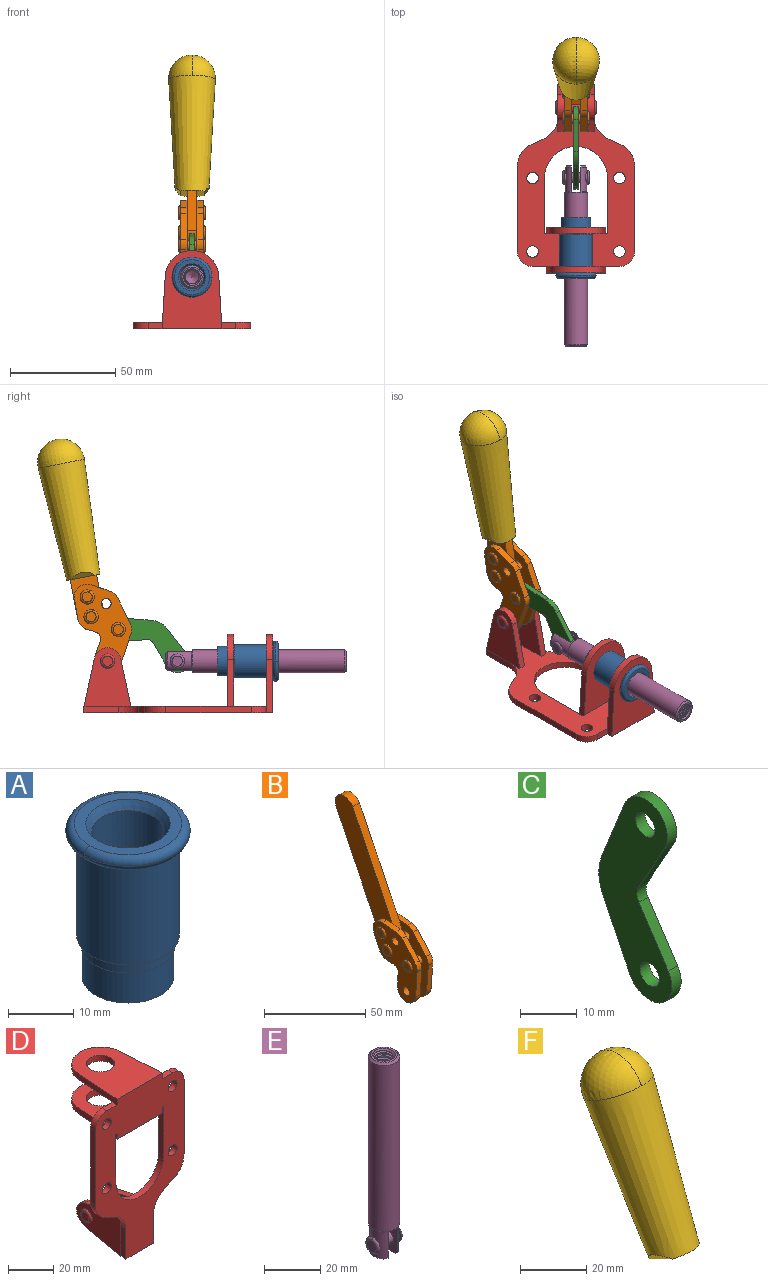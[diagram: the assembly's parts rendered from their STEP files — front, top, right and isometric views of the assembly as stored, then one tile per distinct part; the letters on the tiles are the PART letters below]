
ASSEMBLY  parts=6 mates=6
PART A: 15 faces, bbox 20.6x20.6x28.7 mm
  f0: torus R=8.26mm, axis (0,0,1), area 56.8mm2, adj f1,f10,f12
  f1: torus R=8.26mm, axis (0,0,1), area 56.8mm2, adj f0,f6,f13
  f2: cylinder r=5.59mm len=25.91mm, axis (0,0,1), area 909.6mm2, adj f3,f4
  f3: cone r=6.86mm half-angle=45deg, axis (0,0,-1), area 70.2mm2, adj f2,f14
  f4: cone r=6.47mm half-angle=30deg, axis (0,0,1), area 66.7mm2, adj f2,f13
  f5: cylinder r=7.04mm len=14.07mm, axis (0,0,1), area 252.6mm2, adj f11,f14
  f6: torus R=8.26mm, axis (0,0,1), area 56.8mm2, adj f1,f12,f13
  f7: cylinder r=7.16mm len=14.33mm, axis (0,0,1), area 91.5mm2, adj f9,f11
  f8: cylinder r=7.86mm len=18.42mm, axis (0,0,1), area 909.6mm2, adj f9,f10
  f9: plane 15.72x15.72mm, normal (0,0,-1), area 33mm2, adj f7,f8
  f10: plane 16.51x16.51mm, normal (0,0,-1), area 19.9mm2, adj f0,f8,f12
  f11: plane 14.33x14.33mm, normal (0,0,-1), area 5.7mm2, adj f5,f7
  f12: torus R=8.26mm, axis (0,0,1), area 56.8mm2, adj f0,f6,f10
  f13: plane 16.51x16.51mm, normal (0,0,1), area 82.7mm2, adj f1,f4,f6
  f14: plane 14.07x14.07mm, normal (0,0,-1), area 7.8mm2, adj f3,f5
PART B: 59 faces, bbox 12.9x60.2x99.6 mm
  f0: torus R=2.39mm, axis (-1,0,0), area 14.9mm2, adj f20,f43,f51
  f1: torus R=2.39mm, axis (-1,0,0), area 14.9mm2, adj f19,f42,f51
  f2: torus R=2.39mm, axis (-1,0,0), area 14.9mm2, adj f18,f35,f51
  f3: torus R=2.39mm, axis (-1,0,0), area 14.9mm2, adj f14,f17,f23
  f4: torus R=2.39mm, axis (-1,0,0), area 14.9mm2, adj f13,f16,f23
  f5: torus R=2.39mm, axis (-1,0,0), area 14.9mm2, adj f12,f15,f23
  f6: cylinder r=2.39mm len=4.78mm, axis (1,0,0), area 46.5mm2, adj f48,f50,f51
  f7: cylinder r=2.39mm len=4.78mm, axis (1,0,0), area 46.5mm2, adj f50,f51
  f8: cylinder r=6.35mm len=12.68mm, axis (1,0,0), area 61.8mm2, adj f38,f39,f50,f51
  f9: cylinder r=2.39mm len=4.78mm, axis (-1,0,0), area 70.5mm2, adj f46,f50
  f10: cylinder r=2.39mm len=4.78mm, axis (-1,0,0), area 46.5mm2, adj f23,f45,f46
  f11: cylinder r=2.39mm len=4.78mm, axis (-1,0,0), area 46.5mm2, adj f23,f46
  f12: plane 4.78x4.78mm, normal (1,0,0), area 17.9mm2, adj f5,f15
  f13: plane 4.78x4.78mm, normal (1,0,0), area 17.9mm2, adj f4,f16
  f14: plane 4.78x4.78mm, normal (1,0,0), area 17.9mm2, adj f3,f17
  f15: torus R=2.39mm, axis (-1,0,0), area 14.9mm2, adj f5,f12,f23
  f16: torus R=2.39mm, axis (-1,0,0), area 14.9mm2, adj f4,f13,f23
  f17: torus R=2.39mm, axis (-1,0,0), area 14.9mm2, adj f3,f14,f23
  f18: plane 4.78x4.78mm, normal (-1,0,0), area 17.9mm2, adj f2,f35
  f19: plane 4.78x4.78mm, normal (-1,0,0), area 17.9mm2, adj f1,f42
  f20: plane 4.78x4.78mm, normal (-1,0,0), area 17.9mm2, adj f0,f43
  f21: plane 2.26x0.2mm, normal (1,0,0), area 0.2mm2, adj f31,f44
  f22: plane 2.26x0.2mm, normal (-1,0,0), area 0.2mm2, adj f41,f44
  f23: plane 39.37x30.77mm, normal (1,0,0), area 565.5mm2, adj f3,f4,f5,f10,f11,f15,f16,f17
  f24: cylinder r=6.1mm len=4.15mm, axis (-1,0,0), area 14.7mm2, adj f23,f25,f32,f46
  f25: plane 10.25x9.01mm, normal (0,-0.75,0.66), area 42.3mm2, adj f23,f24,f26,f46
  f26: cylinder r=6.35mm len=4.64mm, axis (-1,0,0), area 15.6mm2, adj f23,f25,f27,f46
  f27: plane 15.84x3.1mm, normal (0,-1,-0.07), area 49.2mm2, adj f23,f26,f28,f46
  f28: cylinder r=6.35mm len=12.68mm, axis (-1,0,0), area 61.8mm2, adj f23,f27,f29,f46
  f29: plane 8.11x3.1mm, normal (0,1,0.07), area 25.2mm2, adj f23,f28,f30,f46
  f30: cylinder r=3.05mm len=3.25mm, axis (-1,0,0), area 14.8mm2, adj f23,f29,f31,f46
  f31: plane 5.99x3.1mm, normal (0,0.07,-1), area 18.6mm2, adj f21,f23,f30,f44,f46
  f32: plane 9.5x3.1mm, normal (0,-0.07,1), area 29.5mm2, adj f23,f24,f33,f46,f47
  f33: cylinder r=6.1mm len=8.63mm, axis (-1,0,0), area 39.1mm2, adj f23,f32,f34,f47
  f34: plane 8.65x3.96mm, normal (0,0.91,-0.42), area 29.5mm2, adj f23,f33,f44,f47
  f35: torus R=2.39mm, axis (-1,0,0), area 14.9mm2, adj f2,f18,f51
  f36: plane 10.25x9.01mm, normal (0,-0.75,0.66), area 42.3mm2, adj f37,f49,f50,f51
  f37: cylinder r=6.35mm len=4.64mm, axis (1,0,0), area 15.6mm2, adj f36,f38,f50,f51
  f38: plane 15.84x3.1mm, normal (0,-1,-0.07), area 49.2mm2, adj f8,f37,f50,f51
  f39: plane 8.11x3.1mm, normal (0,1,0.07), area 25.2mm2, adj f8,f40,f50,f51
  f40: cylinder r=3.05mm len=3.25mm, axis (1,0,0), area 14.8mm2, adj f39,f41,f50,f51
  f41: plane 5.99x3.1mm, normal (0,0.07,-1), area 18.6mm2, adj f22,f40,f44,f50,f51
  f42: torus R=2.39mm, axis (-1,0,0), area 14.9mm2, adj f1,f19,f51
  f43: torus R=2.39mm, axis (-1,0,0), area 14.9mm2, adj f0,f20,f51
  f44: cylinder r=6.35mm len=12.12mm, axis (-1,0,0), area 128.9mm2, adj f21,f22,f23,f31,f34,f41,f46,f47
  f45: plane 2.65x1.35mm, normal (1,0,0), area 1mm2, adj f10,f55
  f46: plane 39.08x20.42mm, normal (-1,0,0), area 412.5mm2, adj f9,f10,f11,f24,f25,f26,f27,f28
  f47: plane 77.62x39.82mm, normal (1,0,0), area 850mm2, adj f32,f33,f34,f44,f53,f54,f55
  f48: plane 2.65x1.35mm, normal (-1,0,0), area 1mm2, adj f6,f55
  f49: cylinder r=6.1mm len=4.15mm, axis (1,0,0), area 14.7mm2, adj f36,f50,f51,f56
  f50: plane 39.08x20.42mm, normal (1,0,0), area 412.5mm2, adj f6,f7,f8,f9,f36,f37,f38,f39
  f51: plane 39.37x30.77mm, normal (-1,0,0), area 565.5mm2, adj f0,f1,f2,f6,f7,f8,f35,f36
  f52: plane 8.65x3.96mm, normal (0,0.91,-0.42), area 29.5mm2, adj f44,f51,f57,f58
  f53: plane 68.49x33.4mm, normal (0,0.9,-0.44), area 358.1mm2, adj f44,f47,f54,f58
  f54: cylinder r=6.35mm len=12.06mm, axis (1,0,0), area 93.7mm2, adj f47,f53,f55,f58
  f55: plane 68.49x33.4mm, normal (0,-0.9,0.44), area 358.1mm2, adj f44,f45,f46,f47,f48,f50,f54,f58
  f56: plane 9.5x3.1mm, normal (0,-0.07,1), area 29.5mm2, adj f49,f50,f51,f57,f58
  f57: cylinder r=6.1mm len=8.63mm, axis (1,0,0), area 39.1mm2, adj f51,f52,f56,f58
  f58: plane 77.62x39.82mm, normal (-1,0,0), area 850mm2, adj f44,f52,f53,f54,f55,f56,f57
PART C: 12 faces, bbox 2.3x18.2x42.8 mm
  f0: cylinder r=2.4mm len=4.8mm, axis (1,0,0), area 34.9mm2, adj f4,f11
  f1: cylinder r=10.41mm len=8.47mm, axis (1,0,0), area 20.2mm2, adj f4,f9,f10,f11
  f2: cylinder r=3.05mm len=3.16mm, axis (1,0,0), area 7.7mm2, adj f4,f6,f7,f11
  f3: cylinder r=2.4mm len=4.8mm, axis (1,0,0), area 34.9mm2, adj f4,f11
  f4: plane 42.81x18.23mm, normal (-1,0,0), area 414.1mm2, adj f0,f1,f2,f3,f5,f6,f7,f8
  f5: cylinder r=5.54mm len=10.67mm, axis (1,0,0), area 41.8mm2, adj f4,f6,f10,f11
  f6: plane 11.66x6.53mm, normal (0,-0.87,-0.49), area 30.9mm2, adj f2,f4,f5,f11
  f7: plane 11.17x7.33mm, normal (0,-0.84,0.55), area 30.9mm2, adj f2,f4,f8,f11
  f8: cylinder r=5.54mm len=10.51mm, axis (1,0,0), area 41.8mm2, adj f4,f7,f9,f11
  f9: plane 13.67x6.67mm, normal (0,0.9,-0.44), area 35.1mm2, adj f1,f4,f8,f11
  f10: plane 14.1x5.7mm, normal (0,0.93,0.37), area 35.1mm2, adj f1,f4,f5,f11
  f11: plane 42.81x18.23mm, normal (1,0,0), area 414.1mm2, adj f0,f1,f2,f3,f5,f6,f7,f8
PART D: 55 faces, bbox 55.7x37.4x89.8 mm
  f0: torus R=2.41mm, axis (-1,0,0), area 15mm2, adj f11,f15,f25
  f1: torus R=2.41mm, axis (-1,0,0), area 15mm2, adj f10,f12,f22
  f2: cylinder r=2.78mm len=5.56mm, axis (0,-1,0), area 54.2mm2, adj f30,f54
  f3: cylinder r=14.99mm len=29.97mm, axis (0,-1,0), area 145.9mm2, adj f30,f49,f53,f54
  f4: cylinder r=2.78mm len=5.56mm, axis (0,-1,0), area 54.2mm2, adj f30,f54
  f5: cylinder r=2.78mm len=5.56mm, axis (0,-1,0), area 54.2mm2, adj f30,f54
  f6: cylinder r=2.78mm len=5.56mm, axis (0,-1,0), area 54.2mm2, adj f30,f54
  f7: cylinder r=6.35mm len=12.7mm, axis (0,0,1), area 123.6mm2, adj f27,f51
  f8: cylinder r=6.35mm len=12.7mm, axis (0,0,-1), area 124.7mm2, adj f21,f35
  f9: cylinder r=2.41mm len=11.18mm, axis (-1,0,0), area 169.4mm2, adj f16,f19
  f10: plane 4.83x4.83mm, normal (1,0,0), area 18.3mm2, adj f1,f12
  f11: plane 4.83x4.83mm, normal (-1,0,0), area 18.3mm2, adj f0,f15
  f12: torus R=2.41mm, axis (-1,0,0), area 15mm2, adj f1,f10,f22
  f13: cylinder r=6.35mm len=12.41mm, axis (1,0,0), area 53.4mm2, adj f18,f19,f22,f23
  f14: cylinder r=6.35mm len=12.41mm, axis (-1,0,0), area 53.4mm2, adj f16,f17,f24,f25
  f15: torus R=2.41mm, axis (-1,0,0), area 15mm2, adj f0,f11,f25
  f16: plane 27.86x22.35mm, normal (1,0,0), area 425.4mm2, adj f9,f14,f17,f24,f30
  f17: plane 22.86x4.97mm, normal (0,0.21,0.98), area 72.5mm2, adj f14,f16,f25,f30
  f18: plane 22.86x4.97mm, normal (0,0.21,0.98), area 72.5mm2, adj f13,f19,f22,f30
  f19: plane 27.86x22.35mm, normal (-1,0,0), area 425.4mm2, adj f9,f13,f18,f23,f30
  f20: cylinder r=12.7mm len=25.35mm, axis (0,0,-1), area 119.8mm2, adj f21,f34,f35,f36
  f21: plane 34.21x28.07mm, normal (0,0,-1), area 702.4mm2, adj f8,f20,f30,f34,f36
  f22: plane 27.96x22.45mm, normal (1,0,0), area 407.2mm2, adj f1,f12,f13,f18,f23,f30,f42,f43
  f23: plane 22.86x4.97mm, normal (0,0.21,-0.98), area 72.5mm2, adj f13,f19,f22,f44
  f24: plane 22.86x4.97mm, normal (0,0.21,-0.98), area 72.5mm2, adj f14,f16,f25,f44
  f25: plane 27.86x22.35mm, normal (-1,0,0), area 407.1mm2, adj f0,f14,f15,f17,f24,f30,f45,f46
  f26: plane 3.1x0.95mm, normal (0,0,-1), area 2.7mm2, adj f30,f49,f50,f54
  f27: plane 34.21x28.07mm, normal (0,0,1), area 702.4mm2, adj f7,f28,f30,f50,f52
  f28: cylinder r=12.7mm len=25.35mm, axis (0,0,1), area 118.8mm2, adj f27,f50,f51,f52
  f29: plane 3.1x0.95mm, normal (0,0,-1), area 2.7mm2, adj f30,f52,f53,f54
  f30: plane 86.54x55.63mm, normal (0,1,0), area 2362.9mm2, adj f2,f3,f4,f5,f6,f16,f17,f18
  f31: plane 40.56x3.1mm, normal (-1,0,0), area 125.7mm2, adj f30,f32,f48,f54
  f32: cylinder r=7.11mm len=7.11mm, axis (0,-1,0), area 34.6mm2, adj f30,f31,f33,f54
  f33: plane 6.67x3.1mm, normal (0,0,1), area 20.4mm2, adj f30,f32,f34,f54
  f34: plane 25.39x3.13mm, normal (-1,0.06,0), area 79.5mm2, adj f20,f21,f33,f35,f54
  f35: plane 37.31x28.45mm, normal (0,0,1), area 789.9mm2, adj f8,f20,f34,f36,f54
  f36: plane 25.39x3.13mm, normal (1,0.06,0), area 79.5mm2, adj f20,f21,f35,f37,f54
  f37: plane 6.67x3.1mm, normal (0,0,1), area 20.4mm2, adj f30,f36,f38,f54
  f38: cylinder r=7.11mm len=7.11mm, axis (0,-1,0), area 34.6mm2, adj f30,f37,f39,f54
  f39: plane 40.56x3.1mm, normal (1,0,0), area 125.7mm2, adj f30,f38,f40,f54
  f40: cylinder r=11.18mm len=10.16mm, axis (0,-1,0), area 39.5mm2, adj f30,f39,f41,f54
  f41: plane 6.09x3.1mm, normal (0.42,0,-0.91), area 20.8mm2, adj f30,f40,f42,f54
  f42: cylinder r=11.18mm len=9.41mm, axis (0,-1,0), area 37.2mm2, adj f22,f30,f41,f43,f54
  f43: plane 16.5x3.1mm, normal (1,0,0), area 51.1mm2, adj f22,f42,f44,f54
  f44: plane 17.37x3.1mm, normal (0,0,-1), area 53.8mm2, adj f23,f24,f30,f43,f45,f54
  f45: plane 16.5x3.1mm, normal (-1,0,0), area 51.1mm2, adj f25,f44,f46,f54
  f46: cylinder r=11.18mm len=9.41mm, axis (0,-1,0), area 37.2mm2, adj f25,f30,f45,f47,f54
  f47: plane 6.09x3.1mm, normal (-0.42,0,-0.91), area 20.8mm2, adj f30,f46,f48,f54
  f48: cylinder r=11.18mm len=10.16mm, axis (0,-1,0), area 39.5mm2, adj f30,f31,f47,f54
  f49: plane 26.54x3.1mm, normal (-1,0,0), area 82.3mm2, adj f3,f26,f30,f54
  f50: plane 25.39x3.1mm, normal (1,0.06,0), area 78.8mm2, adj f26,f27,f28,f51,f54
  f51: plane 37.31x28.45mm, normal (0,0,-1), area 789.9mm2, adj f7,f28,f50,f52,f54
  f52: plane 25.39x3.1mm, normal (-1,0.06,0), area 78.8mm2, adj f27,f28,f29,f51,f54
  f53: plane 26.54x3.1mm, normal (1,0,0), area 82.3mm2, adj f3,f29,f30,f54
  f54: plane 89.66x55.63mm, normal (0,-1,0), area 2678.5mm2, adj f2,f3,f4,f5,f6,f26,f29,f31
PART E: 48 faces, bbox 12.6x11.1x86.1 mm
  f0: torus R=2.41mm, axis (-1,0,0), area 15mm2, adj f30,f32,f34
  f1: torus R=2.41mm, axis (-1,0,0), area 15mm2, adj f29,f31,f33
  f2: cylinder r=5.54mm len=72.39mm, axis (0,0,1), area 2518.5mm2, adj f3,f4,f42,f43
  f3: cone r=5.54mm half-angle=45deg, axis (0,0,1), area 7.6mm2, adj f2,f5,f41
  f4: cone r=5.54mm half-angle=45deg, axis (0,0,-1), area 34.9mm2, adj f2,f39
  f5: cylinder r=5.08mm len=11.48mm, axis (0,0,1), area 108.3mm2, adj f3,f7,f8,f41
  f6: cylinder r=2.41mm len=4.83mm, axis (-1,0,0), area 71.2mm2, adj f40,f41
  f7: cylinder r=2.41mm len=4.83mm, axis (-1,0,0), area 7.6mm2, adj f5,f34
  f8: cone r=5.08mm half-angle=45deg, axis (0,0,1), area 10.6mm2, adj f5,f37,f41
  f9: cone r=3.98mm half-angle=45deg, axis (0,0,1), area 17.6mm2, adj f27,f39,f45,f46,f47
  f10: cylinder r=2.41mm len=4.83mm, axis (-1,0,0), area 7.6mm2, adj f33,f38
  f11: cylinder r=3.2mm len=6.4mm, axis (0,0,1), area 78.4mm2, adj f12,f28,f44,f45,f47
  f12: cylinder r=3.2mm len=6.4mm, axis (0,0,1), area 10.5mm2, adj f11,f13,f45,f47
  f13: cylinder r=3.2mm len=6.4mm, axis (0,0,1), area 10.5mm2, adj f12,f14,f45,f47
  f14: cylinder r=3.2mm len=6.4mm, axis (0,0,1), area 10.5mm2, adj f13,f15,f45,f47
  f15: cylinder r=3.2mm len=6.4mm, axis (0,0,1), area 10.5mm2, adj f14,f16,f45,f47
  f16: cylinder r=3.2mm len=6.4mm, axis (0,0,1), area 10.5mm2, adj f15,f17,f45,f47
  f17: cylinder r=3.2mm len=6.4mm, axis (0,0,1), area 10.5mm2, adj f16,f18,f45,f47
  f18: cylinder r=3.2mm len=6.4mm, axis (0,0,1), area 10.5mm2, adj f17,f19,f45,f47
  f19: cylinder r=3.2mm len=6.4mm, axis (0,0,1), area 10.5mm2, adj f18,f20,f45,f47
  f20: cylinder r=3.2mm len=6.4mm, axis (0,0,1), area 10.5mm2, adj f19,f21,f45,f47
  f21: cylinder r=3.2mm len=6.4mm, axis (0,0,1), area 10.5mm2, adj f20,f22,f45,f47
  f22: cylinder r=3.2mm len=6.4mm, axis (0,0,1), area 10.5mm2, adj f21,f23,f45,f47
  f23: cylinder r=3.2mm len=6.4mm, axis (0,0,1), area 10.5mm2, adj f22,f24,f45,f47
  f24: cylinder r=3.2mm len=6.4mm, axis (0,0,1), area 10.5mm2, adj f23,f25,f45,f47
  f25: cylinder r=3.2mm len=6.4mm, axis (0,0,1), area 10.5mm2, adj f24,f26,f45,f47
  f26: cylinder r=3.2mm len=6.4mm, axis (0,0,1), area 10.5mm2, adj f25,f27,f45,f47
  f27: cylinder r=3.2mm len=6.4mm, axis (0,0,1), area 7.4mm2, adj f9,f26,f45,f47
  f28: cone r=3.2mm half-angle=60deg, axis (0,0,1), area 37.2mm2, adj f11
  f29: plane 4.83x4.83mm, normal (-1,0,0), area 18.3mm2, adj f1,f31
  f30: plane 4.83x4.83mm, normal (1,0,0), area 18.3mm2, adj f0,f32
  f31: torus R=2.41mm, axis (-1,0,0), area 15mm2, adj f1,f29,f33
  f32: torus R=2.41mm, axis (-1,0,0), area 15mm2, adj f0,f30,f34
  f33: plane 6.83x6.83mm, normal (1,0,0), area 18.3mm2, adj f1,f10,f31
  f34: plane 6.83x6.83mm, normal (-1,0,0), area 18.3mm2, adj f0,f7,f32
  f35: cone r=5.08mm half-angle=45deg, axis (0,0,1), area 10.6mm2, adj f36,f38,f40
  f36: plane 7.25x1.97mm, normal (0,0,-1), area 10mm2, adj f35,f40
  f37: plane 7.25x1.97mm, normal (0,0,-1), area 10mm2, adj f8,f41
  f38: cylinder r=5.08mm len=11.48mm, axis (0,0,1), area 108.3mm2, adj f10,f35,f40,f42
  f39: plane 9.55x9.55mm, normal (0,0,1), area 22mm2, adj f4,f9
  f40: plane 12.76x10.09mm, normal (1,0,0), area 95.7mm2, adj f6,f35,f36,f38,f42,f43
  f41: plane 12.76x10.09mm, normal (-1,0,0), area 95.7mm2, adj f3,f5,f6,f8,f37,f43
  f42: cone r=5.54mm half-angle=45deg, axis (0,0,1), area 7.6mm2, adj f2,f38,f40
  f43: plane 11.07x4.7mm, normal (0,0,-1), area 50.4mm2, adj f2,f40,f41
  f44: plane 0.89x0.62mm, normal (-1,0,0), area 0.3mm2, adj f11,f45,f46,f47
  f45: bspline ~24.8x7.63mm, area 266.6mm2, adj f9,f11,f12,f13,f14,f15,f16,f17
  f46: bspline ~24.87x7.63mm, area 73.6mm2, adj f9,f44,f45,f47
  f47: bspline ~24.98x7.63mm, area 272.5mm2, adj f9,f11,f12,f13,f14,f15,f16,f17
PART F: 11 faces, bbox 22.3x42.6x64.5 mm
  f0: sphere r=11.13mm, area 411.4mm2, adj f1,f8
  f1: cone r=11.11mm half-angle=3.3deg, axis (0,0.44,0.9), area 3251.8mm2, adj f0,f7,f8,f9,f10
  f2: cylinder r=6.16mm len=11.7mm, axis (1,0,0), area 89.5mm2, adj f3,f4,f5,f6
  f3: plane 60.23x36.75mm, normal (-1,0,0), area 763.6mm2, adj f2,f4,f6,f10
  f4: plane 51.37x25.05mm, normal (0,0.9,-0.44), area 264.2mm2, adj f2,f3,f5,f10
  f5: plane 60.23x36.75mm, normal (1,0,0), area 763.6mm2, adj f2,f4,f6,f10
  f6: plane 51.37x25.05mm, normal (0,-0.9,0.44), area 264.2mm2, adj f2,f3,f5,f10
  f7: plane 9.95x5.95mm, normal (0.71,-0.31,-0.64), area 25.8mm2, adj f1,f10
  f8: sphere r=11.13mm, area 411.4mm2, adj f0,f1
  f9: plane 9.95x5.95mm, normal (-0.71,-0.31,-0.64), area 25.8mm2, adj f1,f10
  f10: plane 14.27x11.38mm, normal (0,-0.44,-0.9), area 106.7mm2, adj f1,f3,f4,f5,f6,f7,f9
PLACE A rot(axis=(1,0,0),90deg) t=(0,1.23,0)mm
PLACE B rot(axis=(1,0,0),15deg) t=(0,1.24,49.24)mm
PLACE C rot(axis=(1,0,0),120.2deg) t=(0,25.94,11.13)mm
PLACE D rot(axis=(1,0,0),90deg) t=(0,1.23,0)mm fixed
PLACE E rot(axis=(1,0,0),90deg) t=(0,15.65,0)mm
PLACE F rot(axis=(1,0,0),15deg) t=(0.01,1.24,49.24)mm
MATE revolute B.f7 <-> D.f0  axis (-1,0,0) through (0,33.32,24.61)mm
MATE revolute C.f3 <-> B.f4  axis (1,0,0) through (0,28.16,39.62)mm
MATE fastened B.f54 <-> F.f2  axis (1,0,0) through (0,55.69,120.54)mm
MATE revolute C.f5 <-> E.f6  axis (1,0,0) through (0,0.18,24.61)mm
MATE fastened D.f7 <-> A.f2  axis (0,-1,0) through (0,-45.16,24.61)mm
MATE slider E.f2 <-> D.f7  axis (0,-1,0) through (0,-43.13,24.61)mm
